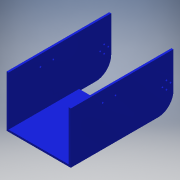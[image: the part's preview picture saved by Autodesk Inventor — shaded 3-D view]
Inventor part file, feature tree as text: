
AUTODESK INVENTOR PART (.ipt)
format: ipt  version: 2016 (Build 200138000, 138)  size: 132,608 bytes
history: native  units: in
note: dims shown in document units (in); Inventor stores cm internally (conversion verified against a paired STEP export)
features: reference x7, sketch x5, extrude x3, hole x2, fillet x1
ambient origin geometry x8: Origin, YZ Plane, XZ Plane, XY Plane, X Axis, Y Axis, Z Axis, Center Point
bodies: Solid1 (feature_tree)
feature tree (18):
  extrude  "Extrusion1"  Depth=8.0in
  extrude  "Extrusion2"  Depth=4.7in
  extrude  "Extrusion3"  Depth=2.5in
  fillet  "Fillet1"  Radius=0.15in
  hole  "Hole3"  [1 undecoded]
  hole  "Hole4"  [1 undecoded]
  sketch  "Sketch1"  dims[d0=5.0in d1=8.0in]
  sketch  "Sketch3"  dims[d2=4.0in d3=0.0in d4=4.7in]
  sketch  "Sketch4"  dims[d5=3.85in d6=0.0in d7=2.5in d8=0.15in d9=0.0in]
  sketch  "Sketch7"  dims[d10=1.2in]
  reference  "Reference13"
  reference  "Reference14"
  reference  "Reference15"
  reference  "Reference16"
  reference  "Reference17"
  sketch  "Sketch8"  dims[d25=0.1457in d26=0.75in d27=0.375in d28=0.25in d29=0.5635in d30=0.15in d31=0.0in d32=0.1457in d33=0.75in d34=0.375in d35=0.25in d36=0.5635in d37=1.0in d38=0.8108in]
  reference  "Reference18"
  reference  "Reference19"
note: 2 required parameter values undecoded (feature->parameter linkage not recoverable at this tier; creation-order binding heuristic only, values carry confidence <= 0.55)
